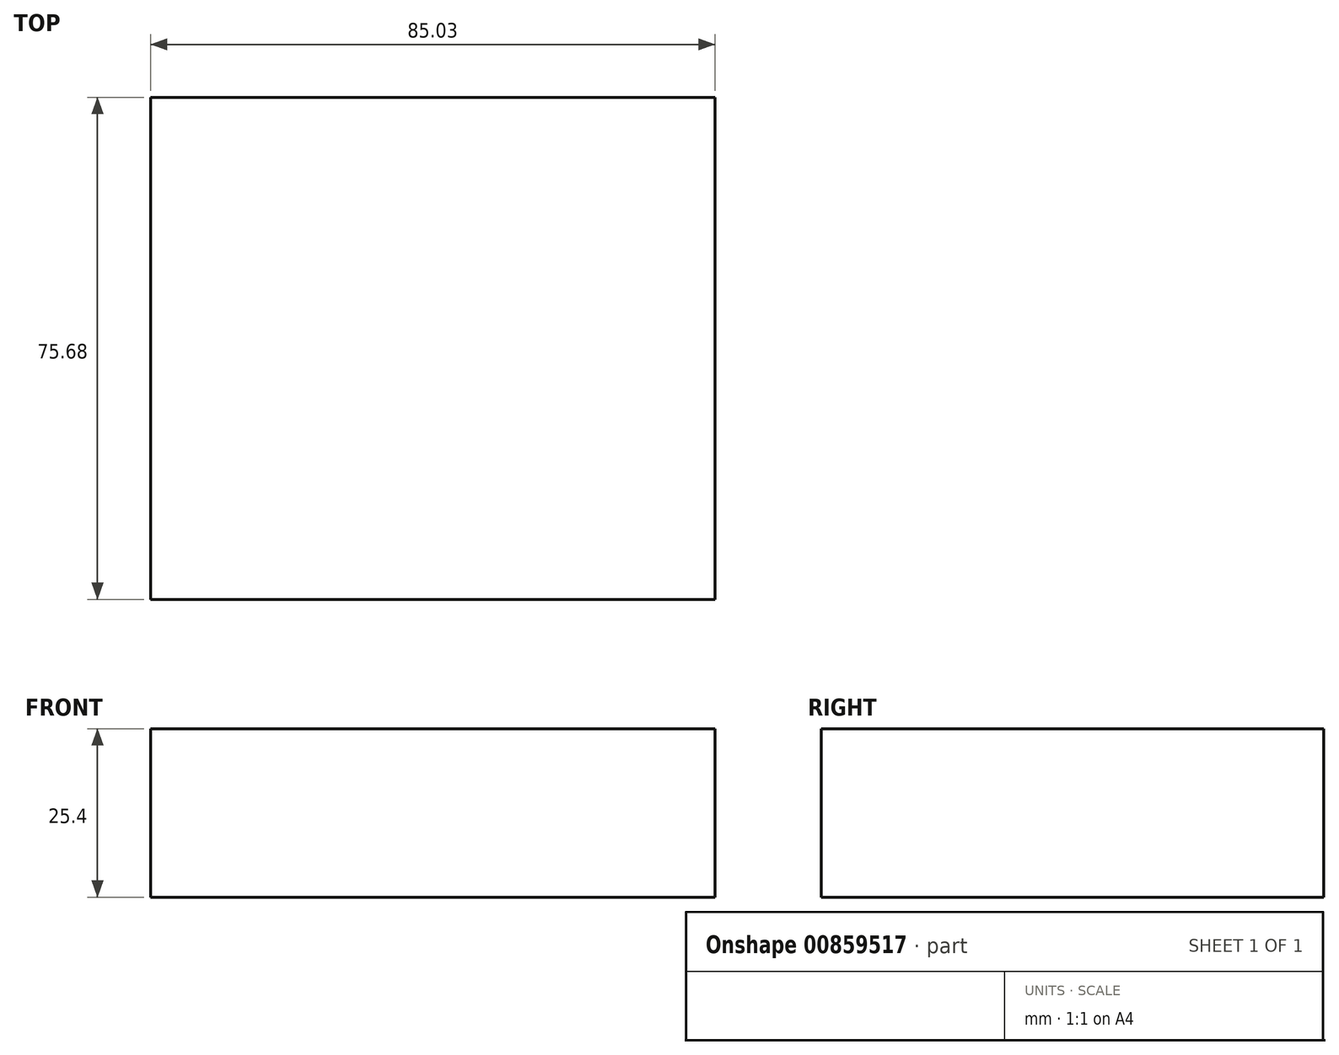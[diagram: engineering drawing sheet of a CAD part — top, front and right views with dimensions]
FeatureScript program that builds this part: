
annotation { "Feature Type Name" : "Feature", "Feature Type Description" : "" }
export const myFeature = defineFeature(function(context is Context, id is Id, definition is map)
    precondition{}
    {
        {
            var Q0;
            Q0=qCreatedBy(makeId("Top.planeOp"),FACE);
            var sketch = newSketch(context, id + "F0", { "sketchPlane" : qUnion([Q0])});
            skLineSegment(sketch, "E0.bottom", {"start": v(-39.42, 32.8) * mm, "end": v(45.6, 32.8) * mm});
            skLineSegment(sketch, "E0.top", {"start": v(-39.42, -42.88) * mm, "end": v(45.6, -42.88) * mm});
            skLineSegment(sketch, "E0.left", {"start": v(-39.42, 32.8) * mm, "end": v(-39.42, -42.88) * mm});
            skLineSegment(sketch, "E0.right", {"start": v(45.6, 32.8) * mm, "end": v(45.6, -42.88) * mm});
            skSolve(sketch);
        }
        {
            var Q0;
            Q0=makeQuery(id+"F0.imprint","IMPRINT",FACE,{"disambiguationData":[TD([[makeQuery(id+"F0.imprint","IMPRINT",EDGE,{"derivedFrom":sQuery(id+"F0.wireOp",EDGE,"E0.bottom")}),-1.0]])]});
            extrude(context, id + "F1", {"entities" : qUnion([Q0]), "depth" : 25.4 * mm, "offsetDistance" : 25.4 * mm});
        }
    });
